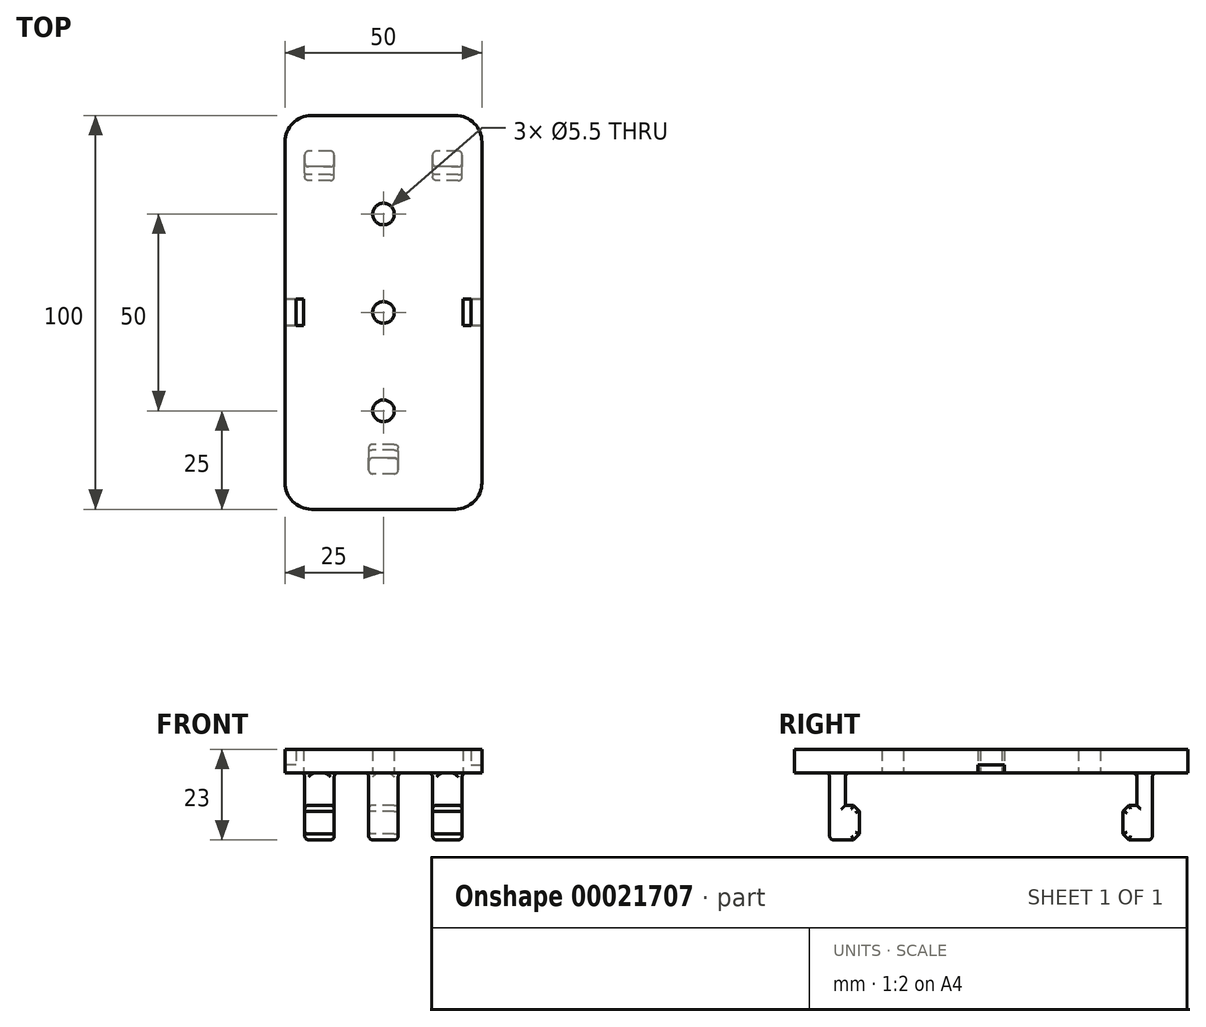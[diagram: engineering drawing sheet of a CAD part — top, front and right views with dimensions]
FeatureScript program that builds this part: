
annotation { "Feature Type Name" : "Feature", "Feature Type Description" : "" }
export const myFeature = defineFeature(function(context is Context, id is Id, definition is map)
    precondition{}
    {
        {
            var Q0;
            Q0=qCreatedBy(makeId("Top.planeOp"),FACE);
            var sketch = newSketch(context, id + "F7", { "sketchPlane" : qUnion([Q0])});
            skLineSegment(sketch, "E0", {"start": v(0, 0) * mm, "end": v(0, 25) * mm, "construction": true});
            skLineSegment(sketch, "E1", {"start": v(0, 0) * mm, "end": v(25, 0) * mm, "construction": true});
            skLineSegment(sketch, "E2", {"start": v(25, 0) * mm, "end": v(25, 18.3) * mm});
            skLineSegment(sketch, "E3", {"start": v(18.3, 25) * mm, "end": v(0, 25) * mm});
            skCircle(sketch, "E4", {"center": v(0, 0) * mm, "radius": 2.75 * mm, "construction": true});
            skLineSegment(sketch, "E5", {"start": v(15, 0) * mm, "end": v(15, 16) * mm, "construction": true});
            skLineSegment(sketch, "E6", {"start": v(15, 16) * mm, "end": v(0, 16) * mm, "construction": true});
            skPoint(sketch, "E7.visualSharp", {"position": v(25, 25) * mm});
            skArc(sketch, "E7.filletArc", {"start": v(25, 18.3) * mm, "mid": v(23.04, 23.04) * mm, "end": v(18.3, 25) * mm});
            skLineSegment(sketch, "E8", {"start": v(10, 0) * mm, "end": v(0, 0) * mm, "construction": true});
            skLineSegment(sketch, "E9", {"start": v(0, 10) * mm, "end": v(0, 0) * mm, "construction": true});
            skArc(sketch, "E10", {"start": v(2.75, 0) * mm, "mid": v(1.94, 1.94) * mm, "end": v(0, 2.75) * mm});
            skArc(sketch, "E11.MirrorCS", {"start": v(-2.75, 0) * mm, "mid": v(-1.94, 1.94) * mm, "end": v(0, 2.75) * mm});
            skLineSegment(sketch, "E12.MirrorCS", {"start": v(-18.3, 25) * mm, "end": v(0, 25) * mm});
            skArc(sketch, "E13.MirrorCS", {"start": v(-25, 18.3) * mm, "mid": v(-23.04, 23.04) * mm, "end": v(-18.3, 25) * mm});
            skLineSegment(sketch, "E14.MirrorCS", {"start": v(-25, 0) * mm, "end": v(-25, 18.3) * mm});
            skLineSegment(sketch, "E15.MirrorCS", {"start": v(-25, 0) * mm, "end": v(-25, -25) * mm});
            skLineSegment(sketch, "E16.MirrorCS", {"start": v(-25, -25) * mm, "end": v(0, -25) * mm, "construction": true});
            skArc(sketch, "E17.MirrorCS", {"start": v(-2.75, 0) * mm, "mid": v(-1.94, -1.94) * mm, "end": v(0, -2.75) * mm});
            skArc(sketch, "E18.MirrorCS", {"start": v(2.75, 0) * mm, "mid": v(1.94, -1.94) * mm, "end": v(0, -2.75) * mm});
            skLineSegment(sketch, "E19.MirrorCS", {"start": v(25, -25) * mm, "end": v(0, -25) * mm, "construction": true});
            skLineSegment(sketch, "E20.MirrorCS", {"start": v(25, 0) * mm, "end": v(25, -25) * mm});
            skPoint(sketch, "E21.orphan", {"position": v(-25, -18.3) * mm});
            skPoint(sketch, "E22.orphan", {"position": v(25, -18.3) * mm});
            skPoint(sketch, "E23.orphan", {"position": v(-18.3, -25) * mm});
            skPoint(sketch, "E24.orphan", {"position": v(18.3, -25) * mm});
            skArc(sketch, "E25.MirrorCS", {"start": v(2.75, -50) * mm, "mid": v(1.94, -48.06) * mm, "end": v(0, -47.25) * mm});
            skLineSegment(sketch, "E26.MirrorCS", {"start": v(10, -50) * mm, "end": v(0, -50) * mm, "construction": true});
            skCircle(sketch, "E27.MirrorC", {"center": v(0, -50) * mm, "radius": 2.75 * mm});
            skArc(sketch, "E28.MirrorCS", {"start": v(-2.75, -50) * mm, "mid": v(-1.94, -48.06) * mm, "end": v(0, -47.25) * mm});
            skPoint(sketch, "E29.MirrorP", {"position": v(25, -75) * mm});
            skLineSegment(sketch, "E30.MirrorCS", {"start": v(0, -50) * mm, "end": v(0, -75) * mm, "construction": true});
            skLineSegment(sketch, "E31.MirrorCS", {"start": v(0, -50) * mm, "end": v(25, -50) * mm, "construction": true});
            skLineSegment(sketch, "E32.MirrorCS", {"start": v(25, -50) * mm, "end": v(25, -68.3) * mm});
            skLineSegment(sketch, "E33.MirrorCS", {"start": v(18.3, -75) * mm, "end": v(0, -75) * mm});
            skLineSegment(sketch, "E34.MirrorCS", {"start": v(15, -50) * mm, "end": v(15, -66) * mm, "construction": true});
            skLineSegment(sketch, "E35.MirrorCS", {"start": v(15, -66) * mm, "end": v(0, -66) * mm, "construction": true});
            skArc(sketch, "E36.MirrorCS", {"start": v(25, -68.3) * mm, "mid": v(23.04, -73.04) * mm, "end": v(18.3, -75) * mm});
            skLineSegment(sketch, "E37.MirrorCS", {"start": v(-18.3, -75) * mm, "end": v(0, -75) * mm});
            skLineSegment(sketch, "E38.MirrorCS", {"start": v(0, -60) * mm, "end": v(0, -50) * mm, "construction": true});
            skPoint(sketch, "E39.MirrorP", {"position": v(-25, -31.7) * mm});
            skArc(sketch, "E40.MirrorCS", {"start": v(-25, -68.3) * mm, "mid": v(-23.04, -73.04) * mm, "end": v(-18.3, -75) * mm});
            skArc(sketch, "E41.MirrorCS", {"start": v(-2.75, -50) * mm, "mid": v(-1.94, -51.94) * mm, "end": v(0, -52.75) * mm});
            skLineSegment(sketch, "E42.MirrorCS", {"start": v(25, -50) * mm, "end": v(25, -25) * mm});
            skArc(sketch, "E43.MirrorCS", {"start": v(2.75, -50) * mm, "mid": v(1.94, -51.94) * mm, "end": v(0, -52.75) * mm});
            skPoint(sketch, "E44.MirrorP", {"position": v(25, -31.7) * mm});
            skLineSegment(sketch, "E45.MirrorCS", {"start": v(-25, -50) * mm, "end": v(-25, -68.3) * mm});
            skLineSegment(sketch, "E46.MirrorCS", {"start": v(-25, -50) * mm, "end": v(-25, -25) * mm});
            skLineSegment(sketch, "E47", {"start": v(22.26, -25) * mm, "end": v(22.26, -21.65) * mm});
            skLineSegment(sketch, "E48", {"start": v(22.26, -21.65) * mm, "end": v(25, -21.65) * mm});
            skLineSegment(sketch, "E49", {"start": v(22.26, -21.65) * mm, "end": v(20.26, -21.65) * mm});
            skLineSegment(sketch, "E50", {"start": v(20.26, -21.65) * mm, "end": v(20.26, -25) * mm});
            skLineSegment(sketch, "E51.MirrorCS", {"start": v(22.26, -28.35) * mm, "end": v(25, -28.35) * mm});
            skLineSegment(sketch, "E52.MirrorCS", {"start": v(22.26, -28.35) * mm, "end": v(20.26, -28.35) * mm});
            skLineSegment(sketch, "E53.MirrorCS", {"start": v(20.26, -28.35) * mm, "end": v(20.26, -25) * mm});
            skLineSegment(sketch, "E54.MirrorCS", {"start": v(22.26, -25) * mm, "end": v(22.26, -28.35) * mm});
            skLineSegment(sketch, "E55.MirrorCS", {"start": v(-20.26, -21.65) * mm, "end": v(-20.26, -25) * mm});
            skLineSegment(sketch, "E56.MirrorCS", {"start": v(-22.26, -21.65) * mm, "end": v(-20.26, -21.65) * mm});
            skLineSegment(sketch, "E57.MirrorCS", {"start": v(-22.26, -25) * mm, "end": v(-22.26, -21.65) * mm});
            skLineSegment(sketch, "E58.MirrorCS", {"start": v(-22.26, -21.65) * mm, "end": v(-25, -21.65) * mm});
            skLineSegment(sketch, "E59.MirrorCS", {"start": v(-22.26, -28.35) * mm, "end": v(-25, -28.35) * mm});
            skLineSegment(sketch, "E60.MirrorCS", {"start": v(-22.26, -28.35) * mm, "end": v(-20.26, -28.35) * mm});
            skLineSegment(sketch, "E61.MirrorCS", {"start": v(-20.25, -28.35) * mm, "end": v(-20.25, -25) * mm});
            skLineSegment(sketch, "E62.MirrorCS", {"start": v(-22.26, -25) * mm, "end": v(-22.26, -28.35) * mm});
            skCircle(sketch, "E63", {"center": v(0, -25) * mm, "radius": 2.75 * mm});
            skSolve(sketch);
        }
        {
            var Q0;
            Q0=makeQuery(id+"F7.imprint","IMPRINT",FACE,{"disambiguationData":[TD([[makeQuery(id+"F7.imprint","IMPRINT",EDGE,{"derivedFrom":sQuery(id+"F7.wireOp",EDGE,"E3")}),1.0]])]});
            var Q1;
            Q1=makeQuery(id+"F7.imprint","IMPRINT",FACE,{"disambiguationData":[TD([[makeQuery(id+"F7.imprint","IMPRINT",EDGE,{"derivedFrom":sQuery(id+"F7.wireOp",EDGE,"E57.MirrorCS")}),1.0]])]});
            var Q2;
            Q2=makeQuery(id+"F7.imprint","IMPRINT",FACE,{"disambiguationData":[TD([[makeQuery(id+"F7.imprint","IMPRINT",EDGE,{"derivedFrom":sQuery(id+"F7.wireOp",EDGE,"E47")}),-1.0]])]});
            extrude(context, id + "F0", {"entities" : qUnion([Q0, Q1, Q2]), "depth" : 6 * mm});
        }
        {
            var Q0;
            {var subQ4=sQuery(id+"F7.wireOp",EDGE,"b7290724-1bae-4ef6-8b0c-be54a274980b0.MirrorCS");Q0=makeQuery(id+"F7.imprint","IMPRINT",FACE,{"disambiguationData":[TD([[makeQuery(id+"F7.imprint","IMPRINT",EDGE,{"derivedFrom":subQ4}),1.0]])]});}
            var Q1;
            Q1=makeQuery(id+"F7.imprint","IMPRINT",FACE,{"disambiguationData":[TD([[makeQuery(id+"F7.imprint","IMPRINT",EDGE,{"derivedFrom":sQuery(id+"F7.wireOp",EDGE,"51ec37f0-b5ac-4bec-b7de-1244f6dcbaef")}),-1.0]])]});
            var Q2;
            Q2=makeQuery(id+"F7.imprint","IMPRINT",FACE,{"disambiguationData":[TD([[makeQuery(id+"F7.imprint","IMPRINT",EDGE,{"derivedFrom":sQuery(id+"F7.wireOp",EDGE,"e9a2be94-56a3-4de4-9768-fda7029a3e886.MirrorCS")}),-1.0]])]});
            var Q3;
            Q3=makeQuery(id+"F7.imprint","IMPRINT",FACE,{"disambiguationData":[TD([[makeQuery(id+"F7.imprint","IMPRINT",EDGE,{"derivedFrom":sQuery(id+"F7.wireOp",EDGE,"e9a2be94-56a3-4de4-9768-fda7029a3e883.MirrorCS")}),1.0]])]});
            var Q4;
            Q4=makeQuery(id+"F7.imprint","IMPRINT",FACE,{"disambiguationData":[TD([[makeQuery(id+"F7.imprint","IMPRINT",EDGE,{"derivedFrom":sQuery(id+"F7.wireOp",EDGE,"E57.MirrorCS")}),1.0]])]});
            var Q5;
            Q5=makeQuery(id+"F7.imprint","IMPRINT",FACE,{"disambiguationData":[TD([[makeQuery(id+"F7.imprint","IMPRINT",EDGE,{"derivedFrom":sQuery(id+"F7.wireOp",EDGE,"E47")}),-1.0]])]});
            extrude(context, id + "F8", {"entities" : qUnion([Q0, Q1, Q2, Q3, Q4, Q5]), "operationType" : NewBodyOperationType.REMOVE, "depth" : 2 * mm});
        }
        {
            var Q0;
            Q0=sQuery(id+"F7.wireOp",EDGE,"E0");
            cPlane(context, id + "F1", {"entities" : qUnion([Q0]), "cplaneType" : CPlaneType.LINE_ANGLE, "offset" : 150 * mm, "angle" : 90 * degree, "width" : 150 * mm, "height" : 150 * mm});
        }
        {
            var Q0;
            Q0=qCreatedBy(id+"F1.planeOp",FACE);
            var sketch = newSketch(context, id + "F2", { "sketchPlane" : qUnion([Q0])});
            skLineSegment(sketch, "E64", {"start": v(16, 0) * mm, "end": v(16, -17) * mm});
            skLineSegment(sketch, "E65", {"start": v(16, -17) * mm, "end": v(10, -17) * mm});
            skLineSegment(sketch, "E66", {"start": v(10, -17) * mm, "end": v(8.49, -15.49) * mm});
            skLineSegment(sketch, "E67", {"start": v(8.49, -15.49) * mm, "end": v(8.49, -9.7) * mm});
            skLineSegment(sketch, "E68", {"start": v(8.49, -9.7) * mm, "end": v(10, -8.2) * mm});
            skLineSegment(sketch, "E69", {"start": v(10, -8.2) * mm, "end": v(12, -8.2) * mm});
            skLineSegment(sketch, "E70", {"start": v(12, -8.2) * mm, "end": v(12, 0) * mm});
            skLineSegment(sketch, "E71", {"start": v(8.49, -9.7) * mm, "end": v(5.6, -12.6) * mm, "construction": true});
            skLineSegment(sketch, "E72", {"start": v(5.6, -12.6) * mm, "end": v(8.49, -15.49) * mm, "construction": true});
            skLineSegment(sketch, "E73", {"start": v(8.49, -12.6) * mm, "end": v(5.6, -12.6) * mm, "construction": true});
            skLineSegment(sketch, "E74", {"start": v(12, 0) * mm, "end": v(16, 0) * mm});
            skLineSegment(sketch, "E75", {"start": v(-25, 0) * mm, "end": v(-25, -15.8) * mm, "construction": true});
            skLineSegment(sketch, "E76.MirrorCS", {"start": v(-66, 0) * mm, "end": v(-66, -17) * mm});
            skLineSegment(sketch, "E77.MirrorCS", {"start": v(-62, -8.2) * mm, "end": v(-62, 0) * mm});
            skLineSegment(sketch, "E78.MirrorCS", {"start": v(-58.49, -9.7) * mm, "end": v(-55.6, -12.6) * mm});
            skLineSegment(sketch, "E79.MirrorCS", {"start": v(-60, -8.2) * mm, "end": v(-62, -8.2) * mm});
            skLineSegment(sketch, "E80.MirrorCS", {"start": v(-58.49, -12.6) * mm, "end": v(-55.6, -12.6) * mm});
            skLineSegment(sketch, "E81.MirrorCS", {"start": v(-55.6, -12.6) * mm, "end": v(-58.49, -15.49) * mm});
            skLineSegment(sketch, "E82.MirrorCS", {"start": v(-58.49, -15.49) * mm, "end": v(-58.49, -9.7) * mm});
            skLineSegment(sketch, "E83.MirrorCS", {"start": v(-62, 0) * mm, "end": v(-66, 0) * mm});
            skLineSegment(sketch, "E84.MirrorCS", {"start": v(-58.49, -9.7) * mm, "end": v(-60, -8.2) * mm});
            skLineSegment(sketch, "E85.MirrorCS", {"start": v(-60, -17) * mm, "end": v(-58.49, -15.49) * mm});
            skLineSegment(sketch, "E86.MirrorCS", {"start": v(-66, -17) * mm, "end": v(-60, -17) * mm});
            skSolve(sketch);
        }
        {
            var Q0;
            Q0=makeQuery(id+"F2.imprint","IMPRINT",FACE,{"disambiguationData":[TD([[makeQuery(id+"F2.imprint","IMPRINT",EDGE,{"derivedFrom":sQuery(id+"F2.wireOp",EDGE,"E64")}),-1.0]])]});
            extrude(context, id + "F3", {"entities" : qUnion([Q0]), "operationType" : NewBodyOperationType.ADD, "endBound" : BoundingType.SYMMETRIC, "depth" : 40 * mm});
        }
        {
            var Q0;
            Q0=makeQuery(id+"F2.imprint","IMPRINT",FACE,{"disambiguationData":[TD([[makeQuery(id+"F2.imprint","IMPRINT",EDGE,{"derivedFrom":sQuery(id+"F2.wireOp",EDGE,"E64")}),-1.0]])]});
            extrude(context, id + "F4", {"entities" : qUnion([Q0]), "operationType" : NewBodyOperationType.REMOVE, "endBound" : BoundingType.SYMMETRIC, "oppositeDirection" : true, "depth" : 25 * mm});
        }
        {
            var Q0;
            Q0=makeQuery(id+"F2.imprint","IMPRINT",FACE,{"disambiguationData":[TD([[makeQuery(id+"F2.imprint","IMPRINT",EDGE,{"derivedFrom":sQuery(id+"F2.wireOp",EDGE,"E76.MirrorCS")}),1.0]])]});
            extrude(context, id + "F5", {"entities" : qUnion([Q0]), "operationType" : NewBodyOperationType.ADD, "endBound" : BoundingType.SYMMETRIC, "depth" : 7.5 * mm});
        }
        {
            var Q0;
            Q0=makeQuery(id+"F5.opExtrude","CAP_FACE",FACE,{"disambiguationData":[OSD([sQuery(id+"F2.wireOp",EDGE,"E76.MirrorCS"),sQuery(id+"F2.wireOp",EDGE,"E77.MirrorCS"),sQuery(id+"F2.wireOp",EDGE,"E79.MirrorCS"),sQuery(id+"F2.wireOp",EDGE,"E82.MirrorCS"),sQuery(id+"F2.wireOp",EDGE,"E83.MirrorCS"),sQuery(id+"F2.wireOp",EDGE,"E84.MirrorCS"),sQuery(id+"F2.wireOp",EDGE,"E85.MirrorCS"),sQuery(id+"F2.wireOp",EDGE,"E86.MirrorCS")])],"isStart":false});
            var Q1;
            Q1=makeQuery(id+"F5.opExtrude","CAP_FACE",FACE,{"disambiguationData":[OSD([sQuery(id+"F2.wireOp",EDGE,"E76.MirrorCS"),sQuery(id+"F2.wireOp",EDGE,"E77.MirrorCS"),sQuery(id+"F2.wireOp",EDGE,"E79.MirrorCS"),sQuery(id+"F2.wireOp",EDGE,"E82.MirrorCS"),sQuery(id+"F2.wireOp",EDGE,"E83.MirrorCS"),sQuery(id+"F2.wireOp",EDGE,"E84.MirrorCS"),sQuery(id+"F2.wireOp",EDGE,"E85.MirrorCS"),sQuery(id+"F2.wireOp",EDGE,"E86.MirrorCS")])],"isStart":true});
            var Q2;
            Q2=makeQuery(id+"F5.opExtrude","SWEPT_FACE",FACE,{"disambiguationData":[OSD([sQuery(id+"F2.wireOp",EDGE,"E76.MirrorCS")])]});
            var Q3;
            Q3=makeQuery(id+"F3.opExtrude","CAP_FACE",FACE,{"disambiguationData":[OSD([sQuery(id+"F2.wireOp",EDGE,"E64"),sQuery(id+"F2.wireOp",EDGE,"E65"),sQuery(id+"F2.wireOp",EDGE,"E66"),sQuery(id+"F2.wireOp",EDGE,"E67"),sQuery(id+"F2.wireOp",EDGE,"E68"),sQuery(id+"F2.wireOp",EDGE,"E69"),sQuery(id+"F2.wireOp",EDGE,"E70"),sQuery(id+"F2.wireOp",EDGE,"E74")])],"isStart":false});
            var Q4;
            Q4=makeQuery(id+"F4.boolean.opBoolean","COPY",FACE,{"derivedFrom":makeQuery(id+"F4.opExtrude","CAP_FACE",FACE,{"disambiguationData":[OSD([sQuery(id+"F2.wireOp",EDGE,"E64"),sQuery(id+"F2.wireOp",EDGE,"E65"),sQuery(id+"F2.wireOp",EDGE,"E66"),sQuery(id+"F2.wireOp",EDGE,"E67"),sQuery(id+"F2.wireOp",EDGE,"E68"),sQuery(id+"F2.wireOp",EDGE,"E69"),sQuery(id+"F2.wireOp",EDGE,"E70"),sQuery(id+"F2.wireOp",EDGE,"E74")])],"isStart":true})});
            var Q5;
            {var subQ0=sQuery(id+"F2.wireOp",EDGE,"E64");var subQ1=sQuery(id+"F2.wireOp",EDGE,"E74");var subQ2=sQuery(id+"F2.wireOp",EDGE,"E65");var subQ3=sQuery(id+"F2.wireOp",EDGE,"E66");var subQ4=sQuery(id+"F2.wireOp",EDGE,"E67");var subQ5=sQuery(id+"F2.wireOp",EDGE,"E68");var subQ6=sQuery(id+"F2.wireOp",EDGE,"E69");var subQ7=sQuery(id+"F2.wireOp",EDGE,"E70");Q5=makeQuery(id+"F4.boolean.opBoolean","SPLIT",FACE,{"disambiguationData":[TD([makeQuery(id+"F3.opExtrude","CAP_FACE",FACE,{"disambiguationData":[OSD([subQ0,subQ2,subQ3,subQ4,subQ5,subQ6,subQ7,subQ1])],"isStart":false})])],"derivedFrom":makeQuery(id+"F3.opExtrude","SWEPT_FACE",FACE,{"disambiguationData":[OSD([subQ0])]})});}
            var Q6;
            Q6=makeQuery(id+"F3.opExtrude","CAP_FACE",FACE,{"disambiguationData":[OSD([sQuery(id+"F2.wireOp",EDGE,"E64"),sQuery(id+"F2.wireOp",EDGE,"E65"),sQuery(id+"F2.wireOp",EDGE,"E66"),sQuery(id+"F2.wireOp",EDGE,"E67"),sQuery(id+"F2.wireOp",EDGE,"E68"),sQuery(id+"F2.wireOp",EDGE,"E69"),sQuery(id+"F2.wireOp",EDGE,"E70"),sQuery(id+"F2.wireOp",EDGE,"E74")])],"isStart":true});
            var Q7;
            {var subQ0=sQuery(id+"F2.wireOp",EDGE,"E64");var subQ1=sQuery(id+"F2.wireOp",EDGE,"E74");var subQ2=sQuery(id+"F2.wireOp",EDGE,"E65");var subQ3=sQuery(id+"F2.wireOp",EDGE,"E66");var subQ4=sQuery(id+"F2.wireOp",EDGE,"E67");var subQ5=sQuery(id+"F2.wireOp",EDGE,"E68");var subQ6=sQuery(id+"F2.wireOp",EDGE,"E69");var subQ7=sQuery(id+"F2.wireOp",EDGE,"E70");Q7=makeQuery(id+"F4.boolean.opBoolean","SPLIT",FACE,{"disambiguationData":[TD([makeQuery(id+"F3.opExtrude","CAP_FACE",FACE,{"disambiguationData":[OSD([subQ0,subQ2,subQ3,subQ4,subQ5,subQ6,subQ7,subQ1])],"isStart":true})])],"derivedFrom":makeQuery(id+"F3.opExtrude","SWEPT_FACE",FACE,{"disambiguationData":[OSD([subQ0])]})});}
            var Q8;
            Q8=makeQuery(id+"F4.boolean.opBoolean","COPY",FACE,{"derivedFrom":makeQuery(id+"F4.opExtrude","CAP_FACE",FACE,{"disambiguationData":[OSD([sQuery(id+"F2.wireOp",EDGE,"E64"),sQuery(id+"F2.wireOp",EDGE,"E65"),sQuery(id+"F2.wireOp",EDGE,"E66"),sQuery(id+"F2.wireOp",EDGE,"E67"),sQuery(id+"F2.wireOp",EDGE,"E68"),sQuery(id+"F2.wireOp",EDGE,"E69"),sQuery(id+"F2.wireOp",EDGE,"E70"),sQuery(id+"F2.wireOp",EDGE,"E74")])],"isStart":false})});
            fillet(context, id + "F6", {"entities" : qUnion([Q0, Q1, Q2, Q3, Q4, Q5, Q6, Q7, Q8]), "radius" : 1 * mm, "tangentPropagation" : true, "allowEdgeOverflow" : false});
        }
    });
